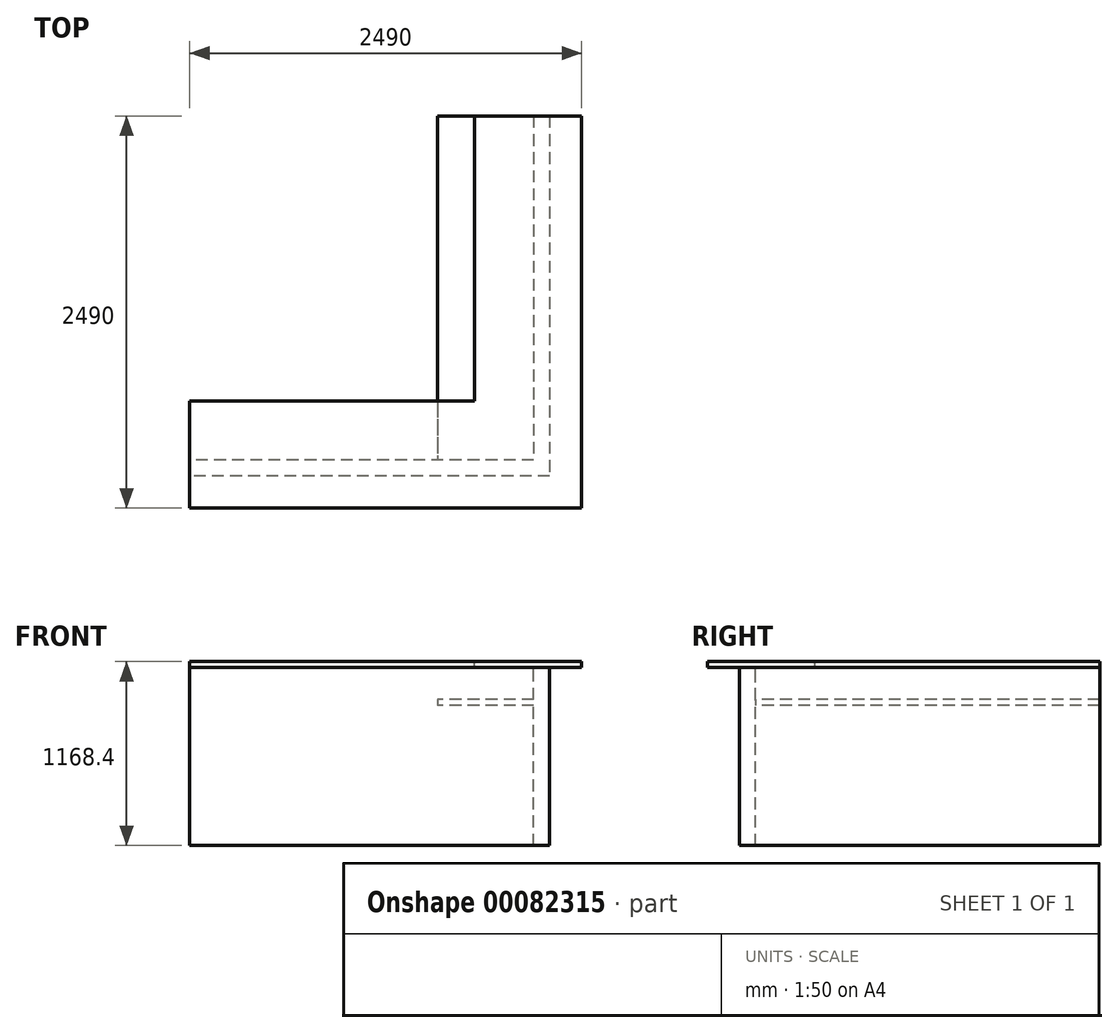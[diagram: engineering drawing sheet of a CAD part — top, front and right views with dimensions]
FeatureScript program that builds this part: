
annotation { "Feature Type Name" : "Feature", "Feature Type Description" : "" }
export const myFeature = defineFeature(function(context is Context, id is Id, definition is map)
    precondition{}
    {
        {
            var Q0;
            Q0=qCreatedBy(makeId("Top.planeOp"),FACE);
            var sketch = newSketch(context, id + "F0", { "sketchPlane" : qUnion([Q0])});
            skLineSegment(sketch, "E0", {"start": v(-2490, 650) * mm, "end": v(-2490, 0) * mm, "construction": true});
            skLineSegment(sketch, "E1", {"start": v(-2490, 0) * mm, "end": v(0, 0) * mm});
            skLineSegment(sketch, "E2", {"start": v(0, 0) * mm, "end": v(0, 2490) * mm});
            skLineSegment(sketch, "E3", {"start": v(0, 2490) * mm, "end": v(-650, 2490) * mm, "construction": true});
            skLineSegment(sketch, "E4", {"start": v(-650, 2490) * mm, "end": v(-650, 650) * mm, "construction": true});
            skLineSegment(sketch, "E5", {"start": v(-650, 650) * mm, "end": v(-2490, 650) * mm, "construction": true});
            skLineSegment(sketch, "E6", {"start": v(-650, 650) * mm, "end": v(0, 0) * mm, "construction": true});
            skLineSegment(sketch, "E7", {"start": v(-2490, 304.8) * mm, "end": v(-2490, 203.2) * mm, "construction": true});
            skLineSegment(sketch, "E8", {"start": v(-2490, 203.2) * mm, "end": v(-203.2, 203.2) * mm, "construction": true});
            skLineSegment(sketch, "E9", {"start": v(-203.2, 203.2) * mm, "end": v(-203.2, 2490) * mm, "construction": true});
            skLineSegment(sketch, "E10", {"start": v(-203.2, 2490) * mm, "end": v(-304.8, 2490) * mm, "construction": true});
            skLineSegment(sketch, "E11", {"start": v(-304.8, 2490) * mm, "end": v(-304.8, 304.8) * mm, "construction": true});
            skLineSegment(sketch, "E12", {"start": v(-304.8, 304.8) * mm, "end": v(-2490, 304.8) * mm, "construction": true});
            skSolve(sketch);
        }
        {
            var Q0;
            Q0=sQuery(id+"F0.wireOp",EDGE,"E3");
            cPlane(context, id + "F1", {"entities" : qUnion([Q0]), "cplaneType" : CPlaneType.LINE_ANGLE, "offset" : 152.4 * mm, "angle" : 0 * degree, "width" : 152.4 * mm, "height" : 152.4 * mm});
        }
        {
            var Q0;
            Q0=qCreatedBy(id+"F1.planeOp",FACE);
            var sketch = newSketch(context, id + "F2", { "sketchPlane" : qUnion([Q0])});
            skLineSegment(sketch, "E13", {"start": v(-203.2, 1130.3) * mm, "end": v(-203.2, 0) * mm});
            skLineSegment(sketch, "E14", {"start": v(-203.2, 0) * mm, "end": v(-304.8, 0) * mm});
            skLineSegment(sketch, "E15", {"start": v(-304.8, 0) * mm, "end": v(-304.8, 889) * mm});
            skLineSegment(sketch, "E16", {"start": v(-304.8, 889) * mm, "end": v(-914.4, 889) * mm});
            skLineSegment(sketch, "E17", {"start": v(-914.4, 889) * mm, "end": v(-914.4, 927.1) * mm});
            skLineSegment(sketch, "E18", {"start": v(-914.4, 927.1) * mm, "end": v(-304.8, 927.1) * mm});
            skLineSegment(sketch, "E19", {"start": v(-304.8, 927.1) * mm, "end": v(-304.8, 1130.3) * mm});
            skLineSegment(sketch, "E20", {"start": v(-304.8, 1130.3) * mm, "end": v(-680, 1130.3) * mm});
            skLineSegment(sketch, "E21", {"start": v(-680, 1130.3) * mm, "end": v(-680, 1168.4) * mm});
            skLineSegment(sketch, "E22", {"start": v(-680, 1168.4) * mm, "end": v(0, 1168.4) * mm});
            skLineSegment(sketch, "E23", {"start": v(0, 1168.4) * mm, "end": v(0, 1130.3) * mm});
            skLineSegment(sketch, "E24", {"start": v(0, 1130.3) * mm, "end": v(-203.2, 1130.3) * mm});
            skLineSegment(sketch, "E25", {"start": v(-304.8, 927.1) * mm, "end": v(-304.8, 889) * mm, "construction": true});
            skSolve(sketch);
        }
        {
            var Q0;
            Q0=makeQuery(id+"F2.imprint","IMPRINT",FACE,{"disambiguationData":[TD([[makeQuery(id+"F2.imprint","IMPRINT",EDGE,{"derivedFrom":sQuery(id+"F2.wireOp",EDGE,"E13")}),-1.0]])]});
            var Q1;
            Q1=sQuery(id+"F0.wireOp",EDGE,"E2");
            var Q2;
            Q2=sQuery(id+"F0.wireOp",EDGE,"E1");
            sweep(context, id + "F3", {"profiles" : qUnion([Q0]), "path" : qUnion([Q1, Q2])});
        }
        {
            var Q0;
            Q0=makeQuery(id+"F3.opSweep","SWEPT_FACE",FACE,{"disambiguationData":[OSD([sQuery(id+"F0.wireOp",EDGE,"E1"),sQuery(id+"F2.wireOp",EDGE,"E17")])]});
            var sketch = newSketch(context, id + "F4", { "sketchPlane" : qUnion([Q0])});
            skLineSegment(sketch, "E26.bottom", {"start": v(914.4, 927.1) * mm, "end": v(2490, 927.1) * mm});
            skLineSegment(sketch, "E26.top", {"start": v(914.4, 889) * mm, "end": v(2490, 889) * mm});
            skLineSegment(sketch, "E26.left", {"start": v(914.4, 927.1) * mm, "end": v(914.4, 889) * mm});
            skLineSegment(sketch, "E26.right", {"start": v(2490, 927.1) * mm, "end": v(2490, 889) * mm});
            skSolve(sketch);
        }
        {
            var Q0;
            Q0=makeQuery(id+"F4.imprint","IMPRINT",FACE,{"disambiguationData":[TD([[makeQuery(id+"F4.imprint","IMPRINT",EDGE,{"derivedFrom":sQuery(id+"F4.wireOp",EDGE,"E26.bottom")}),-1.0]])]});
            var Q1;
            Q1=makeQuery(id+"F3.opSweep","SWEPT_FACE",FACE,{"disambiguationData":[OSD([sQuery(id+"F0.wireOp",EDGE,"E1"),sQuery(id+"F2.wireOp",EDGE,"E19")])]});
            extrude(context, id + "F5", {"entities" : qUnion([Q0]), "operationType" : NewBodyOperationType.REMOVE, "endBound" : BoundingType.UP_TO_SURFACE, "oppositeDirection" : true, "endBoundEntityFace" : qUnion([Q1]), "depth" : 25.4 * mm});
        }
    });
